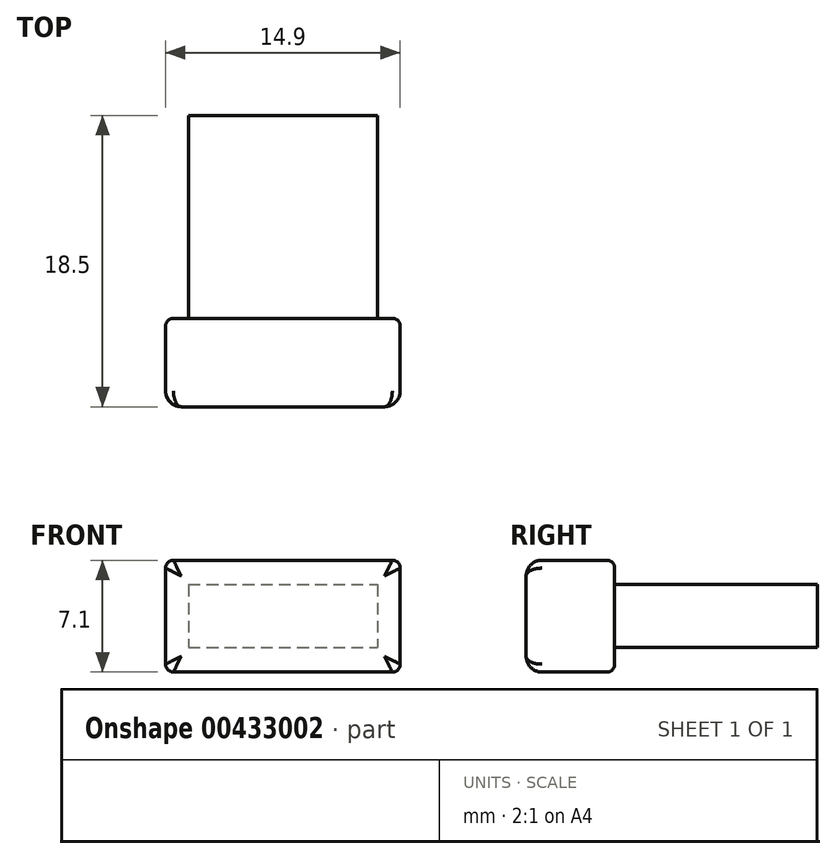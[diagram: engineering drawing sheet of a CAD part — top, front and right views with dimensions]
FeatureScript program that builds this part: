
annotation { "Feature Type Name" : "Feature", "Feature Type Description" : "" }
export const myFeature = defineFeature(function(context is Context, id is Id, definition is map)
    precondition{}
    {
        {
            var Q0;
            Q0=qCreatedBy(makeId("Front.planeOp"),FACE);
            var sketch = newSketch(context, id + "F0", { "sketchPlane" : qUnion([Q0])});
            skLineSegment(sketch, "E0.bottom", {"start": v(-6, 2) * mm, "end": v(6, 2) * mm});
            skLineSegment(sketch, "E0.top", {"start": v(-6, -2) * mm, "end": v(6, -2) * mm});
            skLineSegment(sketch, "E0.left", {"start": v(-6, 2) * mm, "end": v(-6, -2) * mm});
            skLineSegment(sketch, "E0.right", {"start": v(6, 2) * mm, "end": v(6, -2) * mm});
            skPoint(sketch, "E0.middle", {"position": v(0, 0) * mm});
            skSolve(sketch);
        }
        {
            var Q0;
            Q0=makeQuery(id+"F0.imprint","IMPRINT",FACE,{"disambiguationData":[TD([[makeQuery(id+"F0.imprint","IMPRINT",EDGE,{"derivedFrom":sQuery(id+"F0.wireOp",EDGE,"E0.bottom")}),-1.0]])]});
            extrude(context, id + "F1", {"entities" : qUnion([Q0]), "depth" : 12.88 * mm});
        }
        {
            var Q0;
            Q0=makeQuery(id+"F1.opExtrude","CAP_FACE",FACE,{"disambiguationData":[OSD([sQuery(id+"F0.wireOp",EDGE,"E0.bottom"),sQuery(id+"F0.wireOp",EDGE,"E0.top"),sQuery(id+"F0.wireOp",EDGE,"E0.left"),sQuery(id+"F0.wireOp",EDGE,"E0.right")])],"isStart":false});
            var sketch = newSketch(context, id + "F2", { "sketchPlane" : qUnion([Q0])});
            skLineSegment(sketch, "E1.bottom", {"start": v(7.45, 3.55) * mm, "end": v(-7.45, 3.55) * mm});
            skLineSegment(sketch, "E1.top", {"start": v(7.45, -3.55) * mm, "end": v(-7.45, -3.55) * mm});
            skLineSegment(sketch, "E1.left", {"start": v(7.45, 3.55) * mm, "end": v(7.45, -3.55) * mm});
            skLineSegment(sketch, "E1.right", {"start": v(-7.45, 3.55) * mm, "end": v(-7.45, -3.55) * mm});
            skPoint(sketch, "E1.middle", {"position": v(0, 0) * mm});
            skSolve(sketch);
        }
        {
            var Q0;
            Q0 = qSketchRegion(id + "F2", true);
            extrude(context, id + "F3", {"entities" : qUnion([Q0]), "operationType" : NewBodyOperationType.ADD, "depth" : 5.62 * mm});
        }
        {
            var Q0;
            Q0=makeQuery(id+"F3.opExtrude","CAP_EDGE",EDGE,{"disambiguationData":[OSD([sQuery(id+"F2.wireOp",EDGE,"E1.bottom")])],"isStart":false});
            var Q1;
            Q1=makeQuery(id+"F3.opExtrude","CAP_EDGE",EDGE,{"disambiguationData":[OSD([sQuery(id+"F2.wireOp",EDGE,"E1.left")])],"isStart":false});
            var Q2;
            Q2=makeQuery(id+"F3.opExtrude","CAP_EDGE",EDGE,{"disambiguationData":[OSD([sQuery(id+"F2.wireOp",EDGE,"E1.top")])],"isStart":false});
            var Q3;
            Q3=makeQuery(id+"F3.opExtrude","CAP_EDGE",EDGE,{"disambiguationData":[OSD([sQuery(id+"F2.wireOp",EDGE,"E1.right")])],"isStart":false});
            fillet(context, id + "F4", {"entities" : qUnion([Q0, Q1, Q2, Q3]), "radius" : 1 * mm, "tangentPropagation" : true, "allowEdgeOverflow" : false});
        }
        {
            var Q0;
            Q0=makeQuery(id+"F3.opExtrude","CAP_EDGE",EDGE,{"disambiguationData":[OSD([sQuery(id+"F2.wireOp",EDGE,"E1.bottom")])],"isStart":true});
            var Q1;
            Q1=makeQuery(id+"F3.opExtrude","CAP_EDGE",EDGE,{"disambiguationData":[OSD([sQuery(id+"F2.wireOp",EDGE,"E1.right")])],"isStart":true});
            var Q2;
            Q2=makeQuery(id+"F3.opExtrude","CAP_EDGE",EDGE,{"disambiguationData":[OSD([sQuery(id+"F2.wireOp",EDGE,"E1.top")])],"isStart":true});
            var Q3;
            Q3=makeQuery(id+"F3.opExtrude","CAP_EDGE",EDGE,{"disambiguationData":[OSD([sQuery(id+"F2.wireOp",EDGE,"E1.left")])],"isStart":true});
            var Q4;
            Q4=makeQuery(id+"F3.opExtrude","SWEPT_EDGE",EDGE,{"disambiguationData":[OSD([sQuery(id+"F2.wireOp",EDGE,"E1.bottom"),sQuery(id+"F2.wireOp",EDGE,"E1.left")])]});
            var Q5;
            Q5=makeQuery(id+"F3.opExtrude","SWEPT_EDGE",EDGE,{"disambiguationData":[OSD([sQuery(id+"F2.wireOp",EDGE,"E1.top"),sQuery(id+"F2.wireOp",EDGE,"E1.left")])]});
            var Q6;
            Q6=makeQuery(id+"F3.opExtrude","SWEPT_EDGE",EDGE,{"disambiguationData":[OSD([sQuery(id+"F2.wireOp",EDGE,"E1.top"),sQuery(id+"F2.wireOp",EDGE,"E1.right")])]});
            var Q7;
            Q7=makeQuery(id+"F3.opExtrude","SWEPT_EDGE",EDGE,{"disambiguationData":[OSD([sQuery(id+"F2.wireOp",EDGE,"E1.bottom"),sQuery(id+"F2.wireOp",EDGE,"E1.right")])]});
            fillet(context, id + "F5", {"entities" : qUnion([Q0, Q1, Q2, Q3, Q4, Q5, Q6, Q7]), "radius" : .5 * mm, "tangentPropagation" : true, "allowEdgeOverflow" : false});
        }
    });
